# Revit family: Door-NanaWall-Cero_III-XXXP_PXXX new
name_source: partatom
category: Doors
revit_build: Autodesk Revit Architecture 2014 (Build: 20140709_2115(x64)
units: mm (PartAtom-declared; Revit-internal decimal feet)

## types (1)
- Cero_III- XXXP_PXXX_Configuration
    Actual Height = 7' - 0"
    Actual Panel Width = 2' - 6"
    Actual Width = 7' - 8 71/128"
    Analytic Construction = Metal frame, double/triple glass, glass storm
    Bottom Glazing = 0' - 3 15/16"
    C to C = 0' - 4 11/64"
    C to Ext = 0' - 5 145/256"
    C to Int = 0' - 10 65/256"
    Construction Type = New Construction
    Description = Sliding Glass Wall - XXXP_PXXX Configuration
    Elevation D = No
    Finish = Metal - Nanawall - Clear (anodized)
    Function = Exterior
    Glass Lite Thickness = 0' - 0 1/4"
    Glazing Height = 6' - 4 1/8"
    Glazing Material = Glass - NanaWall - Generic
    Glazing Thickness = 0' - 1 31/32"
    Glazing Width = 2' - 3 153/256"
    Half Thickness = 0' - 0 3/8"
    Heat Transfer Coefficient (U) = 0.49 BTU/(h·ft²·°F)
    Height = 7' - 0"
    Height C = 7' - 0"
    Inset Note = To set Door into wall use Inset parameter found in Instance Properties.
    Installation and Service URL = https://www.nanawall.com
    Manufacturer = NanaWall
    Manufacturer Fax Number = (415) 383-0312
    Model = Cero III - XXXP_PXXX Configuration
    Operation = Sliding
    Panel Height = 6' - 7 25/128"
    Panel Width = 2' - 6"
    Panel Width C = 2' - 6"
    Performance URL = https://www.nanawall.com
    Pocket Length = 2' - 6"
    Product Name = Cero
    Product Page URL = https://www.nanawall.com
    Rough Height = 7' - 0 1/2"
    Rough Offset = 0' - 0 1/2"
    Rough Width = 7' - 9 71/128"
    S Glazing = 0' - 0 111/128"
    Size Note = Contact Nanawall for Larger Sizes
    Sizing Statement = Maximum Panel Size = 7' 4 1/2 (W) x 13' 1 (H) (2250 mm x 4000 mm)
    Solar Heat Gain Coefficient = 0
    Subcategory = Sliding Glass Wall
    Thermal Resistance (R) = 2.0409 (h·ft²·°F)/BTU
    Thickness = 0' - 0 3/4"
    Top Glazing = 0' - 3 15/16"
    URL = https://www.nanawall.com
    Version = 2014-v1.0a
    Visual Light Transmittance = 0
    Wall Closure = By host
    Warranty URL = https://www.nanawall.com
    Width = 7' - 8 71/128"
    Width C = 7' - 8 71/128"

## geometry (parser evidence)
native form markers: Blend x878, Sweep x18
no freeform markers — native parametric forms only
